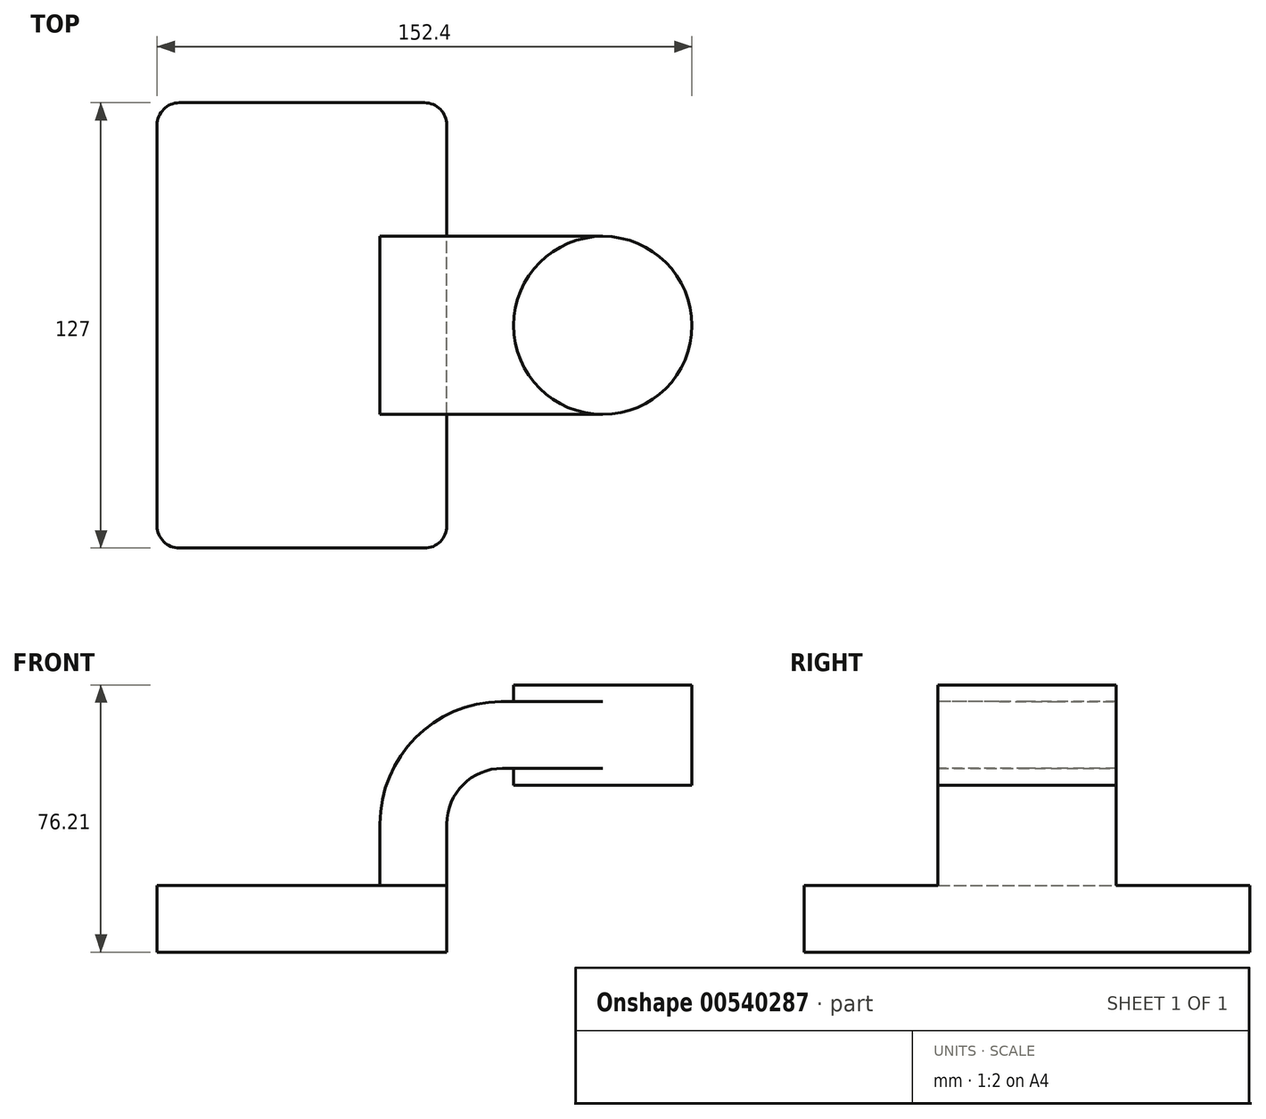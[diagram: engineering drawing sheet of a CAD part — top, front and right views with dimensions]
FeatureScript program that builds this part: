
annotation { "Feature Type Name" : "Feature", "Feature Type Description" : "" }
export const myFeature = defineFeature(function(context is Context, id is Id, definition is map)
    precondition{}
    {
        {
            var Q0;
            Q0=qCreatedBy(makeId("Front.planeOp"),FACE);
            var sketch = newSketch(context, id + "F0", { "sketchPlane" : qUnion([Q0])});
            skLineSegment(sketch, "E0.bottom", {"start": v(41.27, 9.53) * mm, "end": v(-41.28, 9.53) * mm});
            skLineSegment(sketch, "E0.top", {"start": v(41.28, -9.52) * mm, "end": v(-41.27, -9.52) * mm});
            skLineSegment(sketch, "E0.left", {"start": v(41.28, 9.53) * mm, "end": v(41.28, -9.52) * mm});
            skLineSegment(sketch, "E0.right", {"start": v(-41.28, 9.53) * mm, "end": v(-41.28, -9.52) * mm});
            skPoint(sketch, "E0.middle", {"position": v(0, 0) * mm});
            skLineSegment(sketch, "E1.bottom", {"start": v(60.32, 38.1) * mm, "end": v(111.12, 38.1) * mm});
            skLineSegment(sketch, "E1.top", {"start": v(60.32, 66.68) * mm, "end": v(111.12, 66.68) * mm});
            skLineSegment(sketch, "E1.left", {"start": v(60.32, 38.1) * mm, "end": v(60.32, 66.67) * mm});
            skLineSegment(sketch, "E1.right", {"start": v(111.12, 38.1) * mm, "end": v(111.12, 66.67) * mm});
            skPoint(sketch, "E1.middle", {"position": v(85.72, 52.39) * mm});
            skLineSegment(sketch, "E2", {"start": v(41.27, 9.53) * mm, "end": v(41.27, 27) * mm});
            skArc(sketch, "E3", {"start": v(41.27, 27) * mm, "mid": v(45.92, 38.23) * mm, "end": v(57.15, 42.88) * mm});
            skLineSegment(sketch, "E4", {"start": v(57.15, 42.88) * mm, "end": v(85.72, 42.88) * mm});
            skLineSegment(sketch, "E5.0", {"start": v(57.15, 61.93) * mm, "end": v(85.72, 61.93) * mm});
            skArc(sketch, "E5.1", {"start": v(22.22, 27) * mm, "mid": v(32.45, 51.7) * mm, "end": v(57.15, 61.93) * mm});
            skLineSegment(sketch, "E5.2", {"start": v(22.22, 9.53) * mm, "end": v(22.22, 27) * mm});
            skLineSegment(sketch, "E6", {"start": v(85.72, 38.1) * mm, "end": v(85.72, 66.68) * mm});
            skFitSpline(sketch, "E7", {"points": [v(-41.28, 9.53) * mm, v(57.15, 61.93) * mm], "startDerivative": vector(-2.2, 106.82) * mm, "endDerivative": vector(139.28, 0.6) * mm});
            skSolve(sketch);
        }
        {
            var Q0;
            Q0=makeQuery(id+"F0.imprint","IMPRINT",FACE,{"disambiguationData":[TD([[makeQuery(id+"F0.imprint","IMPRINT",EDGE,{"derivedFrom":sQuery(id+"F0.wireOp",EDGE,"E0.top")}),-1.0]])]});
            extrude(context, id + "F1", {"entities" : qUnion([Q0]), "endBound" : BoundingType.SYMMETRIC, "depth" : 127 * mm, "offsetDistance" : 25.4 * mm});
        }
        {
            var Q0;
            {var subQ5=sQuery(id+"F0.wireOp",EDGE,"E2");Q0=makeQuery(id+"F0.imprint","IMPRINT",FACE,{"disambiguationData":[TD([[makeQuery(id+"F0.imprint","IMPRINT",EDGE,{"derivedFrom":subQ5}),1.0]])]});}
            var Q1;
            {var subQ0=sQuery(id+"F0.wireOp",EDGE,"E4");var subQ1=sQuery(id+"F0.wireOp",EDGE,"E1.left");var subQ2=makeQuery(id+"F0.imprint","INTERSECT",VERTEX,{"derivedFrom":[subQ1,subQ0]});Q1=makeQuery(id+"F0.imprint","IMPRINT",FACE,{"disambiguationData":[TD([[makeQuery(id+"F0.imprint","IMPRINT",EDGE,{"disambiguationData":[TD([[subQ2,-1.0]])],"derivedFrom":subQ1}),-1.0]])]});}
            extrude(context, id + "F2", {"entities" : qUnion([Q0, Q1]), "operationType" : NewBodyOperationType.ADD, "endBound" : BoundingType.SYMMETRIC, "depth" : 50.8 * mm, "offsetDistance" : 25.4 * mm});
        }
        {
            var Q0;
            {var subQ0=sQuery(id+"F0.wireOp",EDGE,"E1.right");Q0=makeQuery(id+"F0.imprint","IMPRINT",FACE,{"disambiguationData":[TD([[makeQuery(id+"F0.imprint","IMPRINT",EDGE,{"derivedFrom":subQ0}),1.0]])]});}
            var Q1;
            Q1=sQuery(id+"F0.wireOp",EDGE,"E6");
            revolve(context, id + "F3", {"operationType" : NewBodyOperationType.ADD, "entities" : qUnion([Q0]), "axis" : qUnion([Q1]), "revolveType" : RevolveType.FULL});
        }
        {
            var Q0;
            Q0=makeQuery(id+"F1.opExtrude","CAP_EDGE",EDGE,{"disambiguationData":[OSD([sQuery(id+"F0.wireOp",EDGE,"E0.left")])],"isStart":false});
            var Q1;
            Q1=makeQuery(id+"F1.opExtrude","CAP_EDGE",EDGE,{"disambiguationData":[OSD([sQuery(id+"F0.wireOp",EDGE,"E0.right")])],"isStart":false});
            var Q2;
            Q2=makeQuery(id+"F1.opExtrude","CAP_EDGE",EDGE,{"disambiguationData":[OSD([sQuery(id+"F0.wireOp",EDGE,"E0.left")])],"isStart":true});
            var Q3;
            Q3=makeQuery(id+"F1.opExtrude","CAP_EDGE",EDGE,{"disambiguationData":[OSD([sQuery(id+"F0.wireOp",EDGE,"E0.right")])],"isStart":true});
            fillet(context, id + "F4", {"entities" : qUnion([Q0, Q1, Q2, Q3]), "radius" : 6.35 * mm, "tangentPropagation" : true, "allowEdgeOverflow" : false});
        }
        {
            var Q0;
            {var subQ4=sQuery(id+"F0.wireOp",EDGE,"E5.1");Q0=makeQuery(id+"F0.imprint","IMPRINT",FACE,{"disambiguationData":[TD([[makeQuery(id+"F0.imprint","IMPRINT",EDGE,{"derivedFrom":subQ4}),1.0]])]});}
            extrude(context, id + "F5", {"entities" : qUnion([Q0]), "operationType" : NewBodyOperationType.ADD, "endBound" : BoundingType.SYMMETRIC, "depth" : 15.88 * mm, "offsetDistance" : 25.4 * mm});
        }
    });
